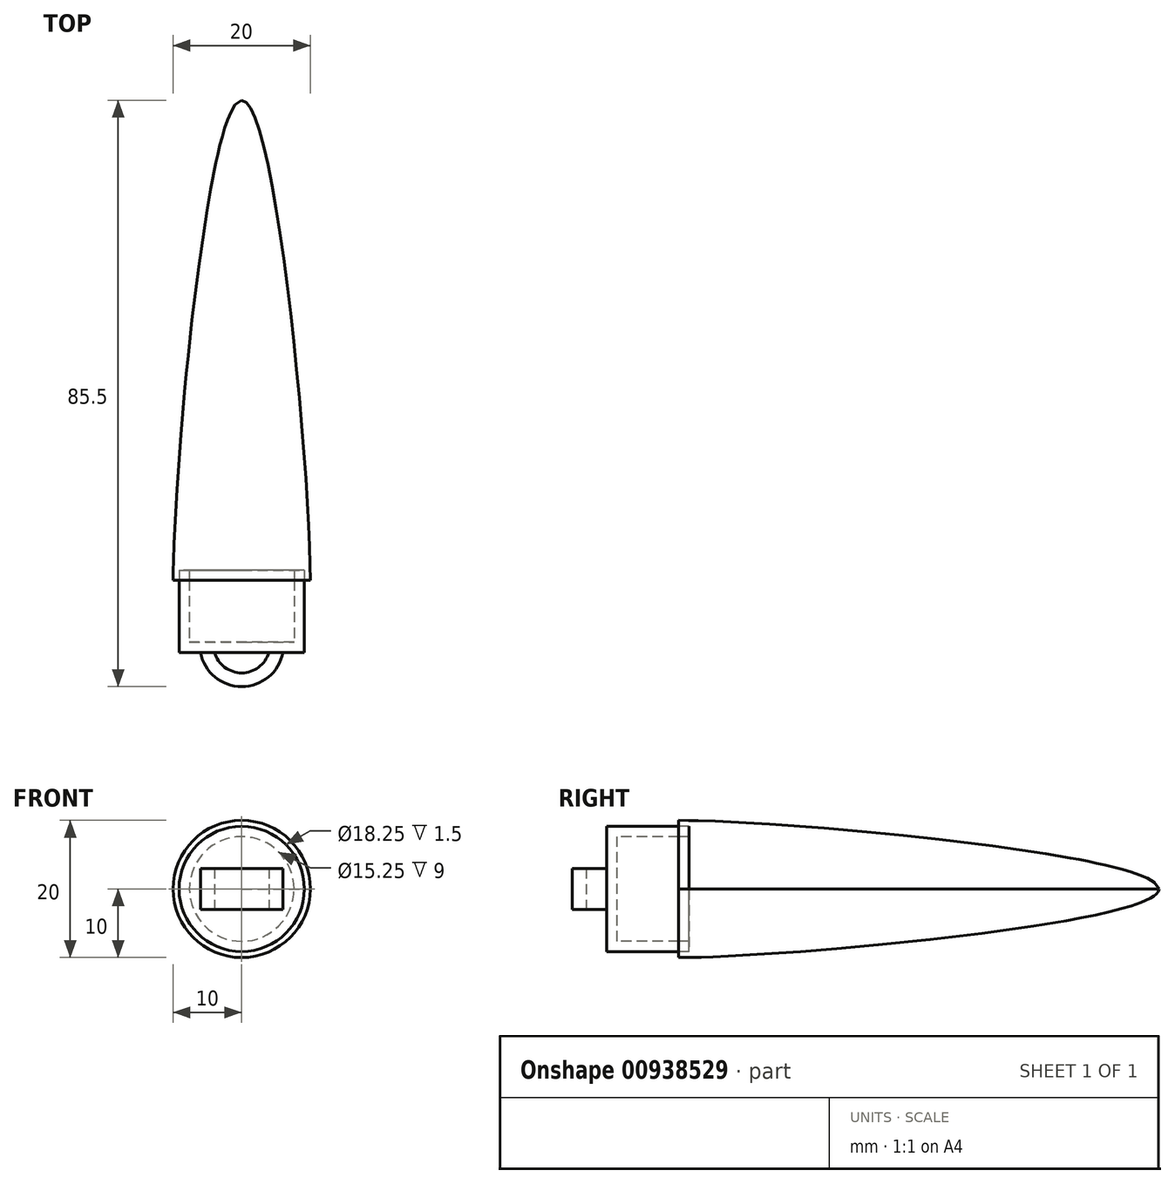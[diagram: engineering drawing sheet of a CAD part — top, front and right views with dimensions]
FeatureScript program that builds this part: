
annotation { "Feature Type Name" : "Feature", "Feature Type Description" : "" }
export const myFeature = defineFeature(function(context is Context, id is Id, definition is map)
    precondition{}
    {
        {
            var Q0;
            Q0=qCreatedBy(makeId("Top.planeOp"),FACE);
            var sketch = newSketch(context, id + "F0", { "sketchPlane" : qUnion([Q0])});
            skLineSegment(sketch, "E0", {"start": v(0, 0) * mm, "end": v(0, 70) * mm});
            skLineSegment(sketch, "E1", {"start": v(0, 0) * mm, "end": v(10, 0) * mm});
            skFitSpline(sketch, "E2", {"points": [v(0, 70) * mm, v(10, 0) * mm], "startDerivative": vector(15, 0) * mm, "endDerivative": vector(0, -48) * mm});
            skFitSpline(sketch, "E3.0", {"points": [v(-0.5, 68.7) * mm, v(-0.49, 68.7) * mm, v(-0.46, 68.67) * mm, v(-0.42, 68.64) * mm, v(-0.4, 68.62) * mm, v(-0.38, 68.61) * mm, v(-0.37, 68.6) * mm, v(-0.37, 68.6) * mm, v(-0.36, 68.6) * mm, v(-0.36, 68.6) * mm, v(-0.36, 68.6) * mm, v(-0.36, 68.6) * mm, v(-0.36, 68.6) * mm, v(-0.36, 68.6) * mm, v(-0.35, 68.58) * mm, v(-0.32, 68.56) * mm, v(-0.28, 68.52) * mm, v(-0.22, 68.44) * mm, v(-0.13, 68.3) * mm, v(0.01, 68.08) * mm, v(0.2, 67.72) * mm, v(0.46, 67.15) * mm, v(0.8, 66.25) * mm, v(1.22, 64.93) * mm, v(1.65, 63.38) * mm, v(2.07, 61.62) * mm, v(2.63, 59.04) * mm, v(3.32, 55.39) * mm, v(4.1, 50.48) * mm, v(4.85, 45.16) * mm, v(5.55, 39.57) * mm, v(6.19, 33.82) * mm, v(6.96, 26.12) * mm, v(7.75, 16.74) * mm, v(8.35, 6.88) * mm, v(8.5, 1.9) * mm, v(8.5, 0) * mm]});
            skLineSegment(sketch, "E4.bottom", {"start": v(7.63, 1.5) * mm, "end": v(9.12, 1.5) * mm});
            skLineSegment(sketch, "E4.top", {"start": v(7.63, -10.5) * mm, "end": v(9.12, -10.5) * mm});
            skLineSegment(sketch, "E4.left", {"start": v(7.63, 1.5) * mm, "end": v(7.63, -10.5) * mm});
            skLineSegment(sketch, "E4.right", {"start": v(9.12, 1.5) * mm, "end": v(9.12, -10.5) * mm});
            skLineSegment(sketch, "E5.bottom", {"start": v(7.63, -10.5) * mm, "end": v(0, -10.5) * mm});
            skLineSegment(sketch, "E5.top", {"start": v(7.62, -9) * mm, "end": v(0, -9) * mm});
            skLineSegment(sketch, "E5.left", {"start": v(7.63, -10.5) * mm, "end": v(7.63, -9) * mm});
            skLineSegment(sketch, "E5.right", {"start": v(0, -10.5) * mm, "end": v(0, -9) * mm});
            skSolve(sketch);
        }
        {
            var Q0;
            {var subQ5=sQuery(id+"F0.wireOp",EDGE,"E2");Q0=makeQuery(id+"F0.imprint","IMPRINT",FACE,{"disambiguationData":[TD([[makeQuery(id+"F0.imprint","IMPRINT",EDGE,{"derivedFrom":subQ5}),-1.0]])]});}
            var Q1;
            {var subQ0=sQuery(id+"F0.wireOp",EDGE,"E3.0");var subQ1=sQuery(id+"F0.wireOp",EDGE,"E1");var subQ2=makeQuery(id+"F0.imprint","INTERSECT",VERTEX,{"derivedFrom":[subQ1,subQ0]});Q1=makeQuery(id+"F0.imprint","IMPRINT",FACE,{"disambiguationData":[TD([[makeQuery(id+"F0.imprint","IMPRINT",EDGE,{"disambiguationData":[TD([[subQ2,1.0]])],"derivedFrom":subQ1}),1.0]])]});}
            var Q2;
            {var subQ0=sQuery(id+"F0.wireOp",EDGE,"E4.top");Q2=makeQuery(id+"F0.imprint","IMPRINT",FACE,{"disambiguationData":[TD([[makeQuery(id+"F0.imprint","IMPRINT",EDGE,{"derivedFrom":subQ0}),1.0]])]});}
            var Q3;
            {var subQ0=sQuery(id+"F0.wireOp",EDGE,"E3.0");var subQ1=sQuery(id+"F0.wireOp",EDGE,"E1");var subQ2=makeQuery(id+"F0.imprint","INTERSECT",VERTEX,{"derivedFrom":[subQ1,subQ0]});Q3=makeQuery(id+"F0.imprint","IMPRINT",FACE,{"disambiguationData":[TD([[makeQuery(id+"F0.imprint","IMPRINT",EDGE,{"disambiguationData":[TD([[subQ2,-1.0]])],"derivedFrom":subQ1}),1.0]])]});}
            var Q4;
            Q4=makeQuery(id+"F0.imprint","IMPRINT",FACE,{"disambiguationData":[TD([[makeQuery(id+"F0.imprint","IMPRINT",EDGE,{"derivedFrom":sQuery(id+"F0.wireOp",EDGE,"E5.bottom")}),-1.0]])]});
            var Q5;
            Q5=sQuery(id+"F0.wireOp",EDGE,"E0");
            revolve(context, id + "F1", {"surfaceOperationType" : NewSurfaceOperationType.NEW, "entities" : qUnion([Q0, Q1, Q2, Q3, Q4]), "axis" : qUnion([Q5]), "revolveType" : RevolveType.FULL});
        }
        {
            var Q0;
            Q0=qCreatedBy(makeId("Top.planeOp"),FACE);
            var sketch = newSketch(context, id + "F2", { "sketchPlane" : qUnion([Q0])});
            skArc(sketch, "E6", {"start": v(-6, -10.5) * mm, "mid": v(0, -15.5) * mm, "end": v(6, -10.5) * mm});
            skArc(sketch, "E7.0", {"start": v(-3.95, -10.5) * mm, "mid": v(0, -13.5) * mm, "end": v(3.95, -10.5) * mm});
            skLineSegment(sketch, "E8", {"start": v(-6, -10.5) * mm, "end": v(6, -10.5) * mm});
            skSolve(sketch);
        }
        {
            var Q0;
            {var subQ0=sQuery(id+"F2.wireOp",EDGE,"E6");Q0=makeQuery(id+"F2.imprint","IMPRINT",FACE,{"disambiguationData":[TD([[makeQuery(id+"F2.imprint","IMPRINT",EDGE,{"derivedFrom":subQ0}),1.0]])]});}
            extrude(context, id + "F3", {"entities" : qUnion([Q0]), "operationType" : NewBodyOperationType.ADD, "endBound" : BoundingType.SYMMETRIC, "depth" : 6 * mm, "offsetDistance" : 25 * mm});
        }
    });
